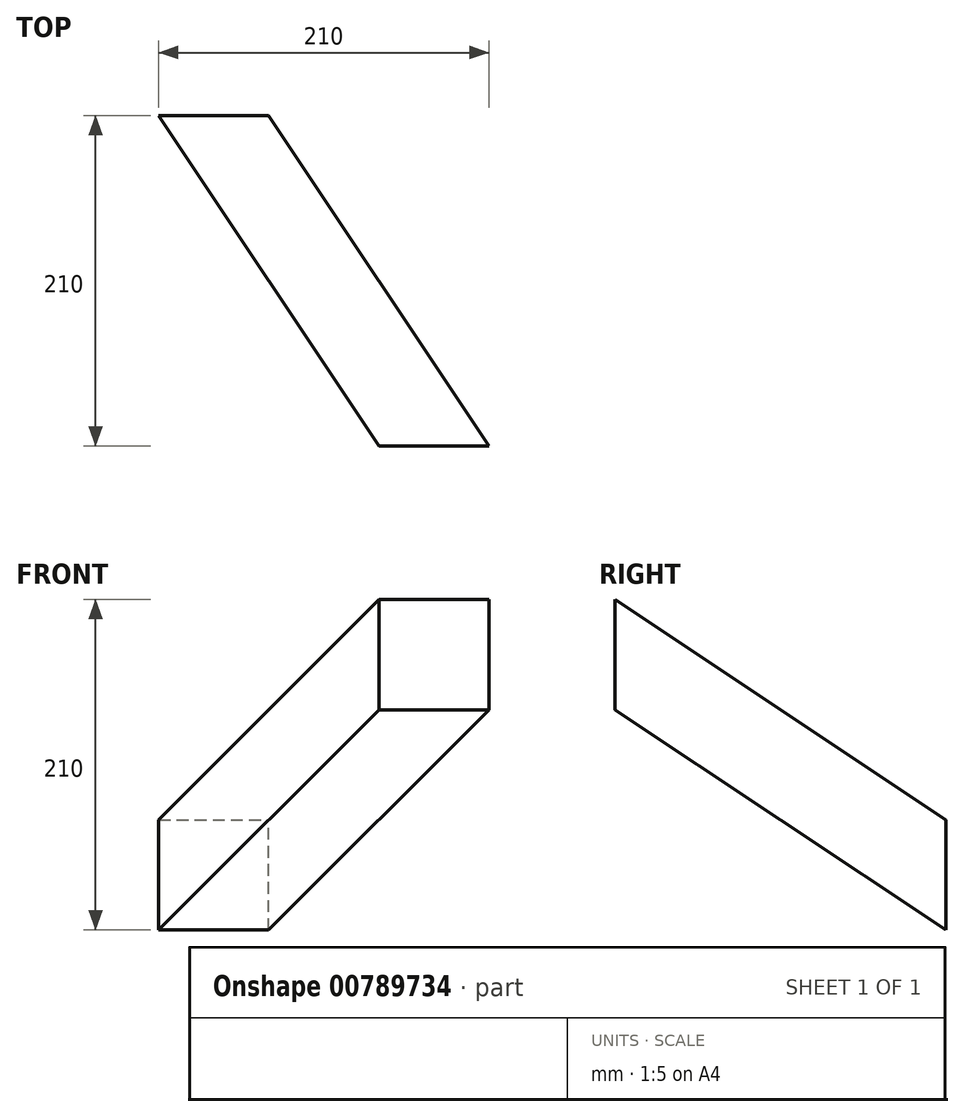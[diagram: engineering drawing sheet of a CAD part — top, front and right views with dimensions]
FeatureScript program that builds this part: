
annotation { "Feature Type Name" : "Feature", "Feature Type Description" : "" }
export const myFeature = defineFeature(function(context is Context, id is Id, definition is map)
    precondition{}
    {
        {
            var Q0;
            Q0=qCreatedBy(makeId("Front.planeOp"),FACE);
            var sketch = newSketch(context, id + "F0", { "sketchPlane" : qUnion([Q0])});
            skLineSegment(sketch, "E0.bottom", {"start": v(0, 0) * mm, "end": v(70, 0) * mm});
            skLineSegment(sketch, "E0.top", {"start": v(0, 70) * mm, "end": v(70, 70) * mm});
            skLineSegment(sketch, "E0.left", {"start": v(0, 0) * mm, "end": v(0, 70) * mm});
            skLineSegment(sketch, "E0.right", {"start": v(70, 0) * mm, "end": v(70, 70) * mm});
            skSolve(sketch);
        }
        {
            var Q0;
            Q0=qCreatedBy(makeId("Front.planeOp"),FACE);
            cPlane(context, id + "F1", {"entities" : qUnion([Q0]), "cplaneType" : CPlaneType.OFFSET, "offset" : 210 * mm, "width" : 152.4 * mm, "height" : 152.4 * mm});
        }
        {
            var Q0;
            Q0=qCreatedBy(id+"F1.planeOp",FACE);
            var sketch = newSketch(context, id + "F2", { "sketchPlane" : qUnion([Q0])});
            skPoint(sketch, "E1.0", {"position": v(70, 70) * mm});
            skLineSegment(sketch, "E2.bottom", {"start": v(70, 70) * mm, "end": v(210, 70) * mm, "construction": true});
            skLineSegment(sketch, "E2.top", {"start": v(70, 210) * mm, "end": v(210, 210) * mm, "construction": true});
            skLineSegment(sketch, "E2.left", {"start": v(70, 70) * mm, "end": v(70, 210) * mm, "construction": true});
            skLineSegment(sketch, "E2.right", {"start": v(210, 70) * mm, "end": v(210, 210) * mm, "construction": true});
            skLineSegment(sketch, "E3", {"start": v(140, 210) * mm, "end": v(140, 70) * mm, "construction": true});
            skLineSegment(sketch, "E4", {"start": v(70, 140) * mm, "end": v(210, 140) * mm, "construction": true});
            skLineSegment(sketch, "E5.bottom", {"start": v(210, 210) * mm, "end": v(140, 210) * mm});
            skLineSegment(sketch, "E5.top", {"start": v(210, 140) * mm, "end": v(140, 140) * mm});
            skLineSegment(sketch, "E5.left", {"start": v(210, 210) * mm, "end": v(210, 140) * mm});
            skLineSegment(sketch, "E5.right", {"start": v(140, 210) * mm, "end": v(140, 140) * mm});
            skSolve(sketch);
        }
        {
            var Q0;
            Q0=makeQuery(id+"F0.imprint","IMPRINT",FACE,{"disambiguationData":[TD([[makeQuery(id+"F0.imprint","IMPRINT",EDGE,{"derivedFrom":sQuery(id+"F0.wireOp",EDGE,"E0.bottom")}),1.0]])]});
            var Q1;
            Q1=makeQuery(id+"F2.imprint","IMPRINT",FACE,{"disambiguationData":[TD([[makeQuery(id+"F2.imprint","IMPRINT",EDGE,{"derivedFrom":sQuery(id+"F2.wireOp",EDGE,"E5.bottom")}),1.0]])]});
            loft(context, id + "F3", {"sheetProfilesArray" : [{ "sheetProfileEntities" : qUnion([Q0]) }, { "sheetProfileEntities" : qUnion([Q1]) }]});
        }
    });
